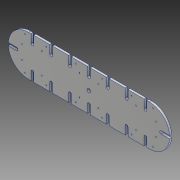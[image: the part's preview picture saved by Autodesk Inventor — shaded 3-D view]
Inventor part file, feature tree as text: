
AUTODESK INVENTOR PART (.ipt)
format: ipt  version: 2020 (Build 240168000, 168)  size: 353,792 bytes
history: native  units: mm
features: plane x3, extrude x3, sketch x2
ambient origin geometry x8: Origin, YZ Plane, XZ Plane, XY Plane, X Axis, Y Axis, Z Axis, Center Point
bodies: Solid1 (feature_tree)
feature tree (8):
  plane  "Work Plane2"
  extrude  "Extrusion2"  Depth=60.0mm
  plane  "Work Plane1"
  extrude  "Extrusion3"  Depth=20.0mm
  plane  "Work Plane3"
  extrude  "Extrusion5"  Depth=10.0mm
  sketch  "Sketch4"  dims[d11=60.0mm d12=60.0mm]
  sketch  "Sketch8"  dims[d14=15.0mm d15=0.0mm d18=20.0mm d21=10.0mm d22=150.0mm d23=150.0mm d24=150.0mm d25=150.0mm d26=150.0mm d27=150.0mm d28=10.0mm d29=10.0mm d30=10.0mm d31=0.0mm d54=76.0mm d55=48.0mm d59=48.0mm d60=76.0mm d73=7.14mm d78=950.0mm d79=240.0mm d80=120.0mm d81=7.14mm d82=7.14mm d83=7.14mm d84=7.14mm d85=190.0mm d86=95.0mm d87=7.14mm d89=7.14mm d91=7.14mm d93=7.14mm d95=10.0mm d96=0.0mm d98=26.0mm d109=135.0mm d110=135.0mm d111=135.0mm d112=135.0mm d113=135.0mm d115=135.0mm d116=20.0mm d120=48.0mm d121=38.0mm d122=38.0mm d123=48.0mm d124=38.0mm d125=38.0mm d130=76.0mm d131=76.0mm d132=1019.0mm d133=210.0mm d134=210.0mm d135=7.14mm d136=7.14mm d137=7.14mm d138=7.14mm d144=76.0mm d145=76.0mm d146=76.0mm d147=76.0mm d149=57.5mm d150=57.5mm d151=57.5mm d152=57.5mm d153=57.5mm d154=57.5mm d155=57.5mm d156=57.5mm]
